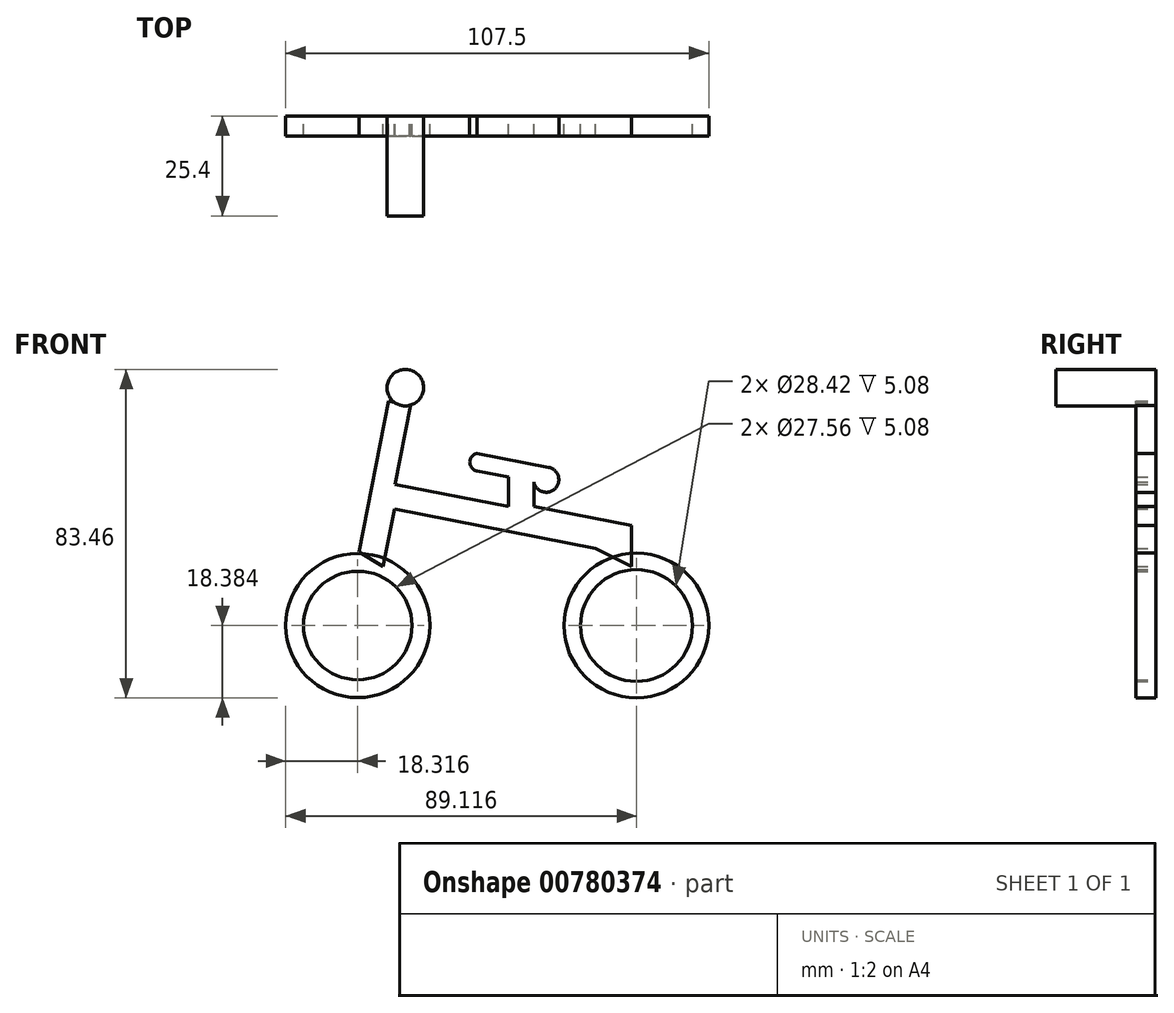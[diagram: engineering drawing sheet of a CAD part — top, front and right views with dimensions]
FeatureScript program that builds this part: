
annotation { "Feature Type Name" : "Feature", "Feature Type Description" : "" }
export const myFeature = defineFeature(function(context is Context, id is Id, definition is map)
    precondition{}
    {
        {
            var Q0;
            Q0=qCreatedBy(makeId("Front.planeOp"),FACE);
            var sketch = newSketch(context, id + "F0", { "sketchPlane" : qUnion([Q0])});
            skCircle(sketch, "E0", {"center": v(-44.75, -26.05) * mm, "radius": 18.32 * mm});
            skCircle(sketch, "E1", {"center": v(26.05, -26.05) * mm, "radius": 18.39 * mm});
            skCircle(sketch, "E2", {"center": v(-44.75, -26.05) * mm, "radius": 13.78 * mm});
            skCircle(sketch, "E3", {"center": v(26.05, -26.05) * mm, "radius": 14.2 * mm});
            skLineSegment(sketch, "E4", {"start": v(26.05, -26.05) * mm, "end": v(29.28, -12.21) * mm});
            skLineSegment(sketch, "E5", {"start": v(26.05, -26.05) * mm, "end": v(21.44, -39.49) * mm});
            skLineSegment(sketch, "E6", {"start": v(26.05, -26.05) * mm, "end": v(39.49, -30.66) * mm});
            skLineSegment(sketch, "E7", {"start": v(26.05, -26.05) * mm, "end": v(12.6, -21.44) * mm});
            skLineSegment(sketch, "E8", {"start": v(26.05, -26.05) * mm, "end": v(12.81, -31.21) * mm});
            skLineSegment(sketch, "E9", {"start": v(26.05, -26.05) * mm, "end": v(31.21, -39.28) * mm});
            skLineSegment(sketch, "E10", {"start": v(26.05, -26.05) * mm, "end": v(20.65, -12.21) * mm});
            skLineSegment(sketch, "E11", {"start": v(26.05, -26.05) * mm, "end": v(39.28, -20.88) * mm});
            skLineSegment(sketch, "E12", {"start": v(-44.75, -26.05) * mm, "end": v(-44.75, -12.26) * mm});
            skLineSegment(sketch, "E13", {"start": v(-44.75, -26.05) * mm, "end": v(-44.75, -39.83) * mm});
            skLineSegment(sketch, "E14", {"start": v(-44.75, -26.05) * mm, "end": v(-58.54, -26.05) * mm});
            skLineSegment(sketch, "E15", {"start": v(-44.75, -26.05) * mm, "end": v(-30.97, -26.05) * mm});
            skLineSegment(sketch, "E16", {"start": v(-44.75, -26.05) * mm, "end": v(-35.34, -15.98) * mm});
            skLineSegment(sketch, "E17", {"start": v(-44.75, -26.05) * mm, "end": v(-54.65, -35.64) * mm});
            skLineSegment(sketch, "E18", {"start": v(-44.75, -26.05) * mm, "end": v(-54.35, -16.15) * mm});
            skLineSegment(sketch, "E19", {"start": v(-44.75, -26.05) * mm, "end": v(-34.5, -35.64) * mm});
            skSolve(sketch);
        }
        {
            var Q0;
            Q0 = qSketchRegion(id + "F0", true);
            extrude(context, id + "F1", {"entities" : qUnion([Q0]), "depth" : 5.08 * mm, "offsetDistance" : 25.4 * mm});
        }
        {
            var Q0;
            Q0 = qSketchRegion(id + "F0", true);
            extrude(context, id + "F2", {"entities" : qUnion([Q0]), "depth" : 5.08 * mm, "offsetDistance" : 25.4 * mm});
        }
        {
            var Q0;
            Q0=qCreatedBy(makeId("Front.planeOp"),FACE);
            var sketch = newSketch(context, id + "F3", { "sketchPlane" : qUnion([Q0])});
            skLineSegment(sketch, "E20", {"start": v(-44.47, -7.34) * mm, "end": v(-36.98, 30.94) * mm});
            skLineSegment(sketch, "E21", {"start": v(-36.98, 30.94) * mm, "end": v(-31.4, 29.85) * mm});
            skLineSegment(sketch, "E22", {"start": v(-31.4, 29.85) * mm, "end": v(-35.3, 9.83) * mm});
            skLineSegment(sketch, "E23", {"start": v(-35.3, 9.83) * mm, "end": v(-6.52, 4.2) * mm});
            skLineSegment(sketch, "E24", {"start": v(-6.52, 4.2) * mm, "end": v(-6.52, 11.66) * mm});
            skLineSegment(sketch, "E25", {"start": v(-6.52, 11.66) * mm, "end": v(0, 10.38) * mm});
            skLineSegment(sketch, "E26", {"start": v(0, 10.38) * mm, "end": v(0, 4.2) * mm});
            skLineSegment(sketch, "E27", {"start": v(0, 4.2) * mm, "end": v(24.8, -0.65) * mm});
            skLineSegment(sketch, "E28", {"start": v(24.8, -0.65) * mm, "end": v(24.8, -6.48) * mm});
            skLineSegment(sketch, "E29", {"start": v(24.8, -6.48) * mm, "end": v(24.8, -11.08) * mm});
            skLineSegment(sketch, "E30", {"start": v(24.8, -11.08) * mm, "end": v(15.69, -6.48) * mm});
            skLineSegment(sketch, "E31", {"start": v(15.69, -6.48) * mm, "end": v(-35.44, 3.52) * mm});
            skLineSegment(sketch, "E32", {"start": v(-35.44, 3.52) * mm, "end": v(-38.3, -11.08) * mm});
            skLineSegment(sketch, "E33", {"start": v(-44.47, -7.34) * mm, "end": v(-38.3, -11.08) * mm});
            skLineSegment(sketch, "E34", {"start": v(-6.52, 11.66) * mm, "end": v(-14.46, 13.2) * mm});
            skArc(sketch, "E35", {"start": v(-14.46, 17.7) * mm, "mid": v(-16.3, 15.45) * mm, "end": v(-14.46, 13.2) * mm});
            skLineSegment(sketch, "E36", {"start": v(-14.46, 17.7) * mm, "end": v(3.75, 14.14) * mm});
            skArc(sketch, "E37", {"start": v(0, 10.38) * mm, "mid": v(5.4, 8.75) * mm, "end": v(3.75, 14.14) * mm});
            skSolve(sketch);
        }
        {
            var Q0;
            Q0 = qSketchRegion(id + "F3", true);
            extrude(context, id + "F4", {"entities" : qUnion([Q0]), "depth" : 5.08 * mm, "offsetDistance" : 25.4 * mm});
        }
        {
            var Q0;
            Q0=qCreatedBy(makeId("Front.planeOp"),FACE);
            var sketch = newSketch(context, id + "F5", { "sketchPlane" : qUnion([Q0])});
            skCircle(sketch, "E38", {"center": v(-32.67, 34.4) * mm, "radius": 4.64 * mm});
            skSolve(sketch);
        }
        {
            var Q0;
            Q0 = qSketchRegion(id + "F5", true);
            extrude(context, id + "F6", {"entities" : qUnion([Q0]), "operationType" : NewBodyOperationType.ADD, "depth" : 25.4 * mm, "offsetDistance" : 25.4 * mm});
        }
    });
